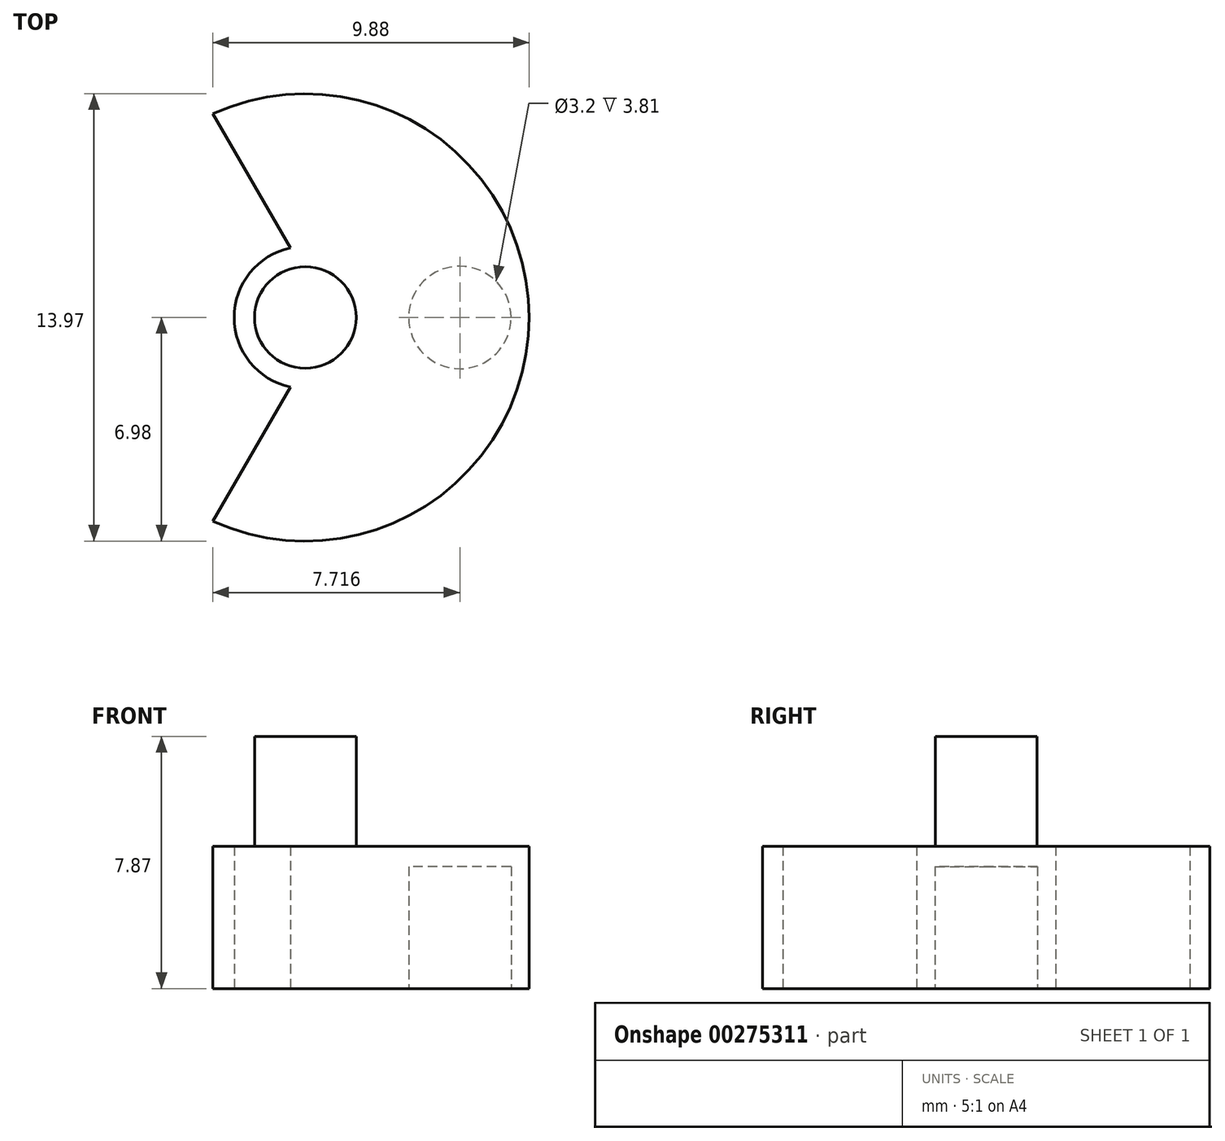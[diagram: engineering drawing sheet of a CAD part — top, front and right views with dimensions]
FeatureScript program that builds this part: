
annotation { "Feature Type Name" : "Feature", "Feature Type Description" : "" }
export const myFeature = defineFeature(function(context is Context, id is Id, definition is map)
    precondition{}
    {
        {
            var Q0;
            Q0=qCreatedBy(makeId("Top.planeOp"),FACE);
            var sketch = newSketch(context, id + "F0", { "sketchPlane" : qUnion([Q0])});
            skArc(sketch, "E0", {"start": v(-2.89, -6.36) * mm, "mid": v(6.98, 0) * mm, "end": v(-2.89, 6.36) * mm});
            skCircle(sketch, "E1", {"center": v(0, 0) * mm, "radius": 1.59 * mm});
            skCircle(sketch, "E2", {"center": v(4.83, 0) * mm, "radius": 1.6 * mm});
            skArc(sketch, "E3", {"start": v(-0.47, 2.17) * mm, "mid": v(-2.22, 0) * mm, "end": v(-0.47, -2.17) * mm});
            skLineSegment(sketch, "E4", {"start": v(0, 0) * mm, "end": v(-6.98, 0) * mm, "construction": true});
            skLineSegment(sketch, "E5", {"start": v(-0.47, 2.17) * mm, "end": v(-2.89, 6.36) * mm});
            skLineSegment(sketch, "E6", {"start": v(-0.47, -2.17) * mm, "end": v(-2.89, -6.36) * mm});
            skSolve(sketch);
        }
        {
            var Q0;
            Q0 = qSketchRegion(id + "F0", true);
            extrude(context, id + "F1", {"entities" : qUnion([Q0]), "depth" : 4.44 * mm});
        }
        {
            var Q0;
            Q0=makeQuery(id+"F1.opExtrude","CAP_FACE",FACE,{"disambiguationData":[OSD([sQuery(id+"F0.wireOp",EDGE,"E0"),sQuery(id+"F0.wireOp",EDGE,"E1"),sQuery(id+"F0.wireOp",EDGE,"E2"),sQuery(id+"F0.wireOp",EDGE,"E3"),sQuery(id+"F0.wireOp",EDGE,"E5"),sQuery(id+"F0.wireOp",EDGE,"E6")])],"isStart":true});
            var sketch = newSketch(context, id + "F2", { "sketchPlane" : qUnion([Q0])});
            skCircle(sketch, "E7.0", {"center": v(0, 0) * mm, "radius": 1.59 * mm});
            skSolve(sketch);
        }
        {
            var Q0;
            Q0 = qSketchRegion(id + "F2", true);
            extrude(context, id + "F3", {"entities" : qUnion([Q0]), "operationType" : NewBodyOperationType.ADD, "oppositeDirection" : true, "depth" : 7.87 * mm});
        }
        {
            var Q0;
            Q0=makeQuery(id+"F1.opExtrude","CAP_FACE",FACE,{"disambiguationData":[OSD([sQuery(id+"F0.wireOp",EDGE,"E0"),sQuery(id+"F0.wireOp",EDGE,"E1"),sQuery(id+"F0.wireOp",EDGE,"E2"),sQuery(id+"F0.wireOp",EDGE,"E3"),sQuery(id+"F0.wireOp",EDGE,"E5"),sQuery(id+"F0.wireOp",EDGE,"E6")])],"isStart":false});
            var sketch = newSketch(context, id + "F4", { "sketchPlane" : qUnion([Q0])});
            skCircle(sketch, "E8.0", {"center": v(4.83, 0) * mm, "radius": 1.6 * mm});
            skSolve(sketch);
        }
        {
            var Q0;
            Q0 = qSketchRegion(id + "F4", true);
            extrude(context, id + "F5", {"entities" : qUnion([Q0]), "operationType" : NewBodyOperationType.ADD, "oppositeDirection" : true, "depth" : 0.64 * mm});
        }
    });
